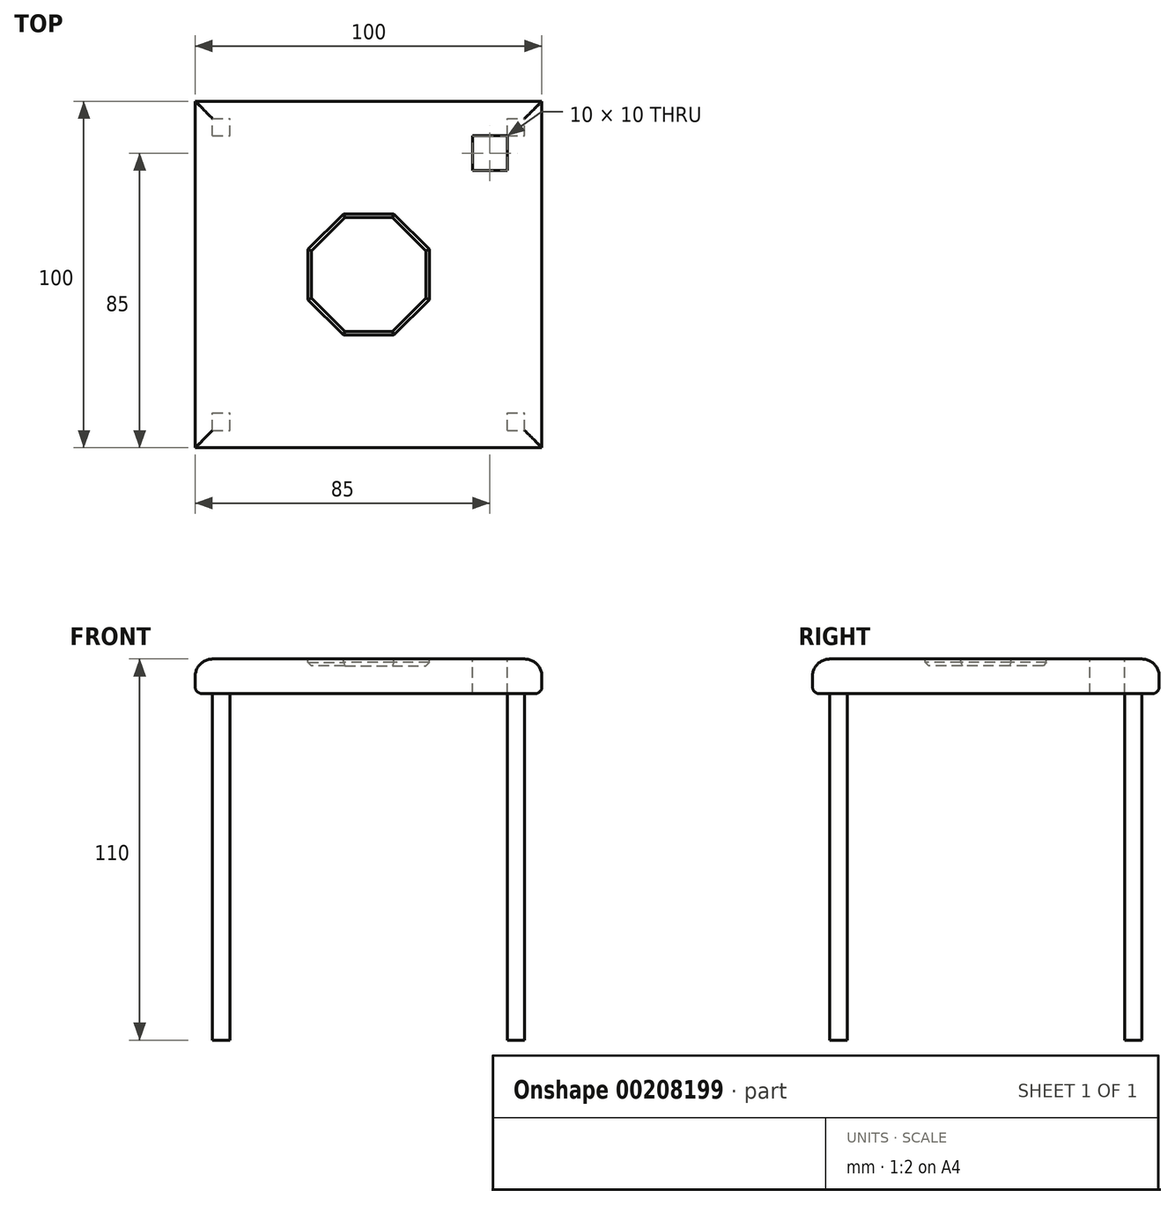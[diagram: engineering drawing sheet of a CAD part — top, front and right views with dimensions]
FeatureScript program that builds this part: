
annotation { "Feature Type Name" : "Feature", "Feature Type Description" : "" }
export const myFeature = defineFeature(function(context is Context, id is Id, definition is map)
    precondition{}
    {
        {
            var Q0;
            Q0=qCreatedBy(makeId("Top.planeOp"),FACE);
            var sketch = newSketch(context, id + "F0", { "sketchPlane" : qUnion([Q0])});
            skLineSegment(sketch, "E0.bottom", {"start": v(-50, 50) * mm, "end": v(50, 50) * mm});
            skLineSegment(sketch, "E0.top", {"start": v(-50, -50) * mm, "end": v(50, -50) * mm});
            skLineSegment(sketch, "E0.left", {"start": v(-50, 50) * mm, "end": v(-50, -50) * mm});
            skLineSegment(sketch, "E0.right", {"start": v(50, 50) * mm, "end": v(50, -50) * mm});
            skSolve(sketch);
        }
        {
            var Q0;
            Q0=makeQuery(id+"F0.imprint","IMPRINT",FACE,{"disambiguationData":[TD([[makeQuery(id+"F0.imprint","IMPRINT",EDGE,{"derivedFrom":sQuery(id+"F0.wireOp",EDGE,"E0.bottom")}),-1.0]])]});
            extrude(context, id + "F1", {"entities" : qUnion([Q0]), "depth" : 10 * mm});
        }
        {
            var Q0;
            Q0=makeQuery(id+"F1.opExtrude","CAP_FACE",FACE,{"disambiguationData":[OSD([sQuery(id+"F0.wireOp",EDGE,"E0.bottom"),sQuery(id+"F0.wireOp",EDGE,"E0.top"),sQuery(id+"F0.wireOp",EDGE,"E0.left"),sQuery(id+"F0.wireOp",EDGE,"E0.right")])],"isStart":true});
            var sketch = newSketch(context, id + "F2", { "sketchPlane" : qUnion([Q0])});
            skLineSegment(sketch, "E1.bottom", {"start": v(-45, 45) * mm, "end": v(-40, 45) * mm});
            skLineSegment(sketch, "E1.top", {"start": v(-45, 40) * mm, "end": v(-40, 40) * mm});
            skLineSegment(sketch, "E1.left", {"start": v(-45, 45) * mm, "end": v(-45, 40) * mm});
            skLineSegment(sketch, "E1.right", {"start": v(-40, 45) * mm, "end": v(-40, 40) * mm});
            skLineSegment(sketch, "E2.0.1.0", {"start": v(-40, -40) * mm, "end": v(-40, -45) * mm});
            skLineSegment(sketch, "E2.0.1.1", {"start": v(-45, -40) * mm, "end": v(-45, -45) * mm});
            skLineSegment(sketch, "E2.0.1.2", {"start": v(-45, -45) * mm, "end": v(-40, -45) * mm});
            skLineSegment(sketch, "E2.0.1.3", {"start": v(-45, -40) * mm, "end": v(-40, -40) * mm});
            skLineSegment(sketch, "E2.1.0.0", {"start": v(45, 45) * mm, "end": v(45, 40) * mm});
            skLineSegment(sketch, "E2.1.0.1", {"start": v(40, 45) * mm, "end": v(40, 40) * mm});
            skLineSegment(sketch, "E2.1.0.2", {"start": v(40, 40) * mm, "end": v(45, 40) * mm});
            skLineSegment(sketch, "E2.1.0.3", {"start": v(40, 45) * mm, "end": v(45, 45) * mm});
            skLineSegment(sketch, "E2.1.1.0", {"start": v(45, -40) * mm, "end": v(45, -45) * mm});
            skLineSegment(sketch, "E2.1.1.1", {"start": v(40, -40) * mm, "end": v(40, -45) * mm});
            skLineSegment(sketch, "E2.1.1.2", {"start": v(40, -45) * mm, "end": v(45, -45) * mm});
            skLineSegment(sketch, "E2.1.1.3", {"start": v(40, -40) * mm, "end": v(45, -40) * mm});
            skLineSegment(sketch, "E2.direction1", {"start": v(-45, 40) * mm, "end": v(40, 40) * mm, "construction": true});
            skLineSegment(sketch, "E2.direction2", {"start": v(-45, 40) * mm, "end": v(-45, -45) * mm, "construction": true});
            skSolve(sketch);
        }
        {
            var Q0;
            Q0 = qSketchRegion(id + "F2", true);
            extrude(context, id + "F3", {"entities" : qUnion([Q0]), "operationType" : NewBodyOperationType.ADD, "depth" : 100 * mm});
        }
        {
            var Q0;
            Q0=makeQuery(id+"F1.opExtrude","CAP_FACE",FACE,{"disambiguationData":[OSD([sQuery(id+"F0.wireOp",EDGE,"E0.bottom"),sQuery(id+"F0.wireOp",EDGE,"E0.top"),sQuery(id+"F0.wireOp",EDGE,"E0.left"),sQuery(id+"F0.wireOp",EDGE,"E0.right")])],"isStart":false});
            fillet(context, id + "F4", {"entities" : qUnion([Q0]), "radius" : 5 * mm, "tangentPropagation" : true, "allowEdgeOverflow" : false});
        }
        {
            var Q0;
            Q0=makeQuery(id+"F1.opExtrude","CAP_EDGE",EDGE,{"disambiguationData":[OSD([sQuery(id+"F0.wireOp",EDGE,"E0.top")])],"isStart":true});
            var Q1;
            Q1=makeQuery(id+"F1.opExtrude","CAP_EDGE",EDGE,{"disambiguationData":[OSD([sQuery(id+"F0.wireOp",EDGE,"E0.right")])],"isStart":true});
            var Q2;
            Q2=makeQuery(id+"F1.opExtrude","CAP_EDGE",EDGE,{"disambiguationData":[OSD([sQuery(id+"F0.wireOp",EDGE,"E0.bottom")])],"isStart":true});
            var Q3;
            Q3=makeQuery(id+"F1.opExtrude","CAP_EDGE",EDGE,{"disambiguationData":[OSD([sQuery(id+"F0.wireOp",EDGE,"E0.left")])],"isStart":true});
            fillet(context, id + "F5", {"entities" : qUnion([Q0, Q1, Q2, Q3]), "radius" : 2 * mm, "tangentPropagation" : true, "allowEdgeOverflow" : false});
        }
        {
            var Q0;
            Q0=makeQuery(id+"F1.opExtrude","CAP_FACE",FACE,{"disambiguationData":[OSD([sQuery(id+"F0.wireOp",EDGE,"E0.bottom"),sQuery(id+"F0.wireOp",EDGE,"E0.top"),sQuery(id+"F0.wireOp",EDGE,"E0.left"),sQuery(id+"F0.wireOp",EDGE,"E0.right")])],"isStart":false});
            var sketch = newSketch(context, id + "F6", { "sketchPlane" : qUnion([Q0])});
            skCircle(sketch, "E3.cCircle", {"center": v(0, 0) * mm, "radius": 17.5 * mm, "construction": true});
            skLineSegment(sketch, "E3.0", {"start": v(7.25, -17.5) * mm, "end": v(-7.25, -17.5) * mm});
            skLineSegment(sketch, "E3.1", {"start": v(-7.25, -17.5) * mm, "end": v(-17.5, -7.25) * mm});
            skLineSegment(sketch, "E3.2", {"start": v(-17.5, -7.25) * mm, "end": v(-17.5, 7.25) * mm});
            skLineSegment(sketch, "E3.3", {"start": v(-17.5, 7.25) * mm, "end": v(-7.25, 17.5) * mm});
            skLineSegment(sketch, "E3.4", {"start": v(-7.25, 17.5) * mm, "end": v(7.25, 17.5) * mm});
            skLineSegment(sketch, "E3.5", {"start": v(7.25, 17.5) * mm, "end": v(17.5, 7.25) * mm});
            skLineSegment(sketch, "E3.6", {"start": v(17.5, 7.25) * mm, "end": v(17.5, -7.25) * mm});
            skLineSegment(sketch, "E3.7", {"start": v(17.5, -7.25) * mm, "end": v(7.25, -17.5) * mm});
            skPoint(sketch, "E3.0.midPoint", {"position": v(0, -17.5) * mm});
            skSolve(sketch);
        }
        {
            var Q0;
            Q0 = qSketchRegion(id + "F6", true);
            extrude(context, id + "F7", {"entities" : qUnion([Q0]), "operationType" : NewBodyOperationType.REMOVE, "oppositeDirection" : true, "depth" : 2 * mm});
        }
        {
            var Q0;
            Q0=makeQuery(id+"F7.boolean.opBoolean","COPY",FACE,{"derivedFrom":makeQuery(id+"F7.opExtrude","CAP_FACE",FACE,{"disambiguationData":[OSD([sQuery(id+"F6.wireOp",EDGE,"E3.0"),sQuery(id+"F6.wireOp",EDGE,"E3.1"),sQuery(id+"F6.wireOp",EDGE,"E3.2"),sQuery(id+"F6.wireOp",EDGE,"E3.3"),sQuery(id+"F6.wireOp",EDGE,"E3.4"),sQuery(id+"F6.wireOp",EDGE,"E3.5"),sQuery(id+"F6.wireOp",EDGE,"E3.6"),sQuery(id+"F6.wireOp",EDGE,"E3.7")])],"isStart":false})});
            chamfer(context, id + "F8", {"entities" : qUnion([Q0]), "width" : 1 * mm, "tangentPropagation" : true});
        }
        {
            var Q0;
            Q0=makeQuery(id+"F1.opExtrude","CAP_FACE",FACE,{"disambiguationData":[OSD([sQuery(id+"F0.wireOp",EDGE,"E0.bottom"),sQuery(id+"F0.wireOp",EDGE,"E0.top"),sQuery(id+"F0.wireOp",EDGE,"E0.left"),sQuery(id+"F0.wireOp",EDGE,"E0.right")])],"isStart":false});
            var sketch = newSketch(context, id + "F9", { "sketchPlane" : qUnion([Q0])});
            skLineSegment(sketch, "E4.bottom", {"start": v(30, 40) * mm, "end": v(40, 40) * mm});
            skLineSegment(sketch, "E4.top", {"start": v(30, 30) * mm, "end": v(40, 30) * mm});
            skLineSegment(sketch, "E4.left", {"start": v(30, 40) * mm, "end": v(30, 30) * mm});
            skLineSegment(sketch, "E4.right", {"start": v(40, 40) * mm, "end": v(40, 30) * mm});
            skSolve(sketch);
        }
        {
            var Q0;
            Q0 = qSketchRegion(id + "F9", true);
            extrude(context, id + "F10", {"entities" : qUnion([Q0]), "operationType" : NewBodyOperationType.REMOVE, "endBound" : BoundingType.UP_TO_NEXT, "oppositeDirection" : true, "depth" : 25 * mm});
        }
    });
